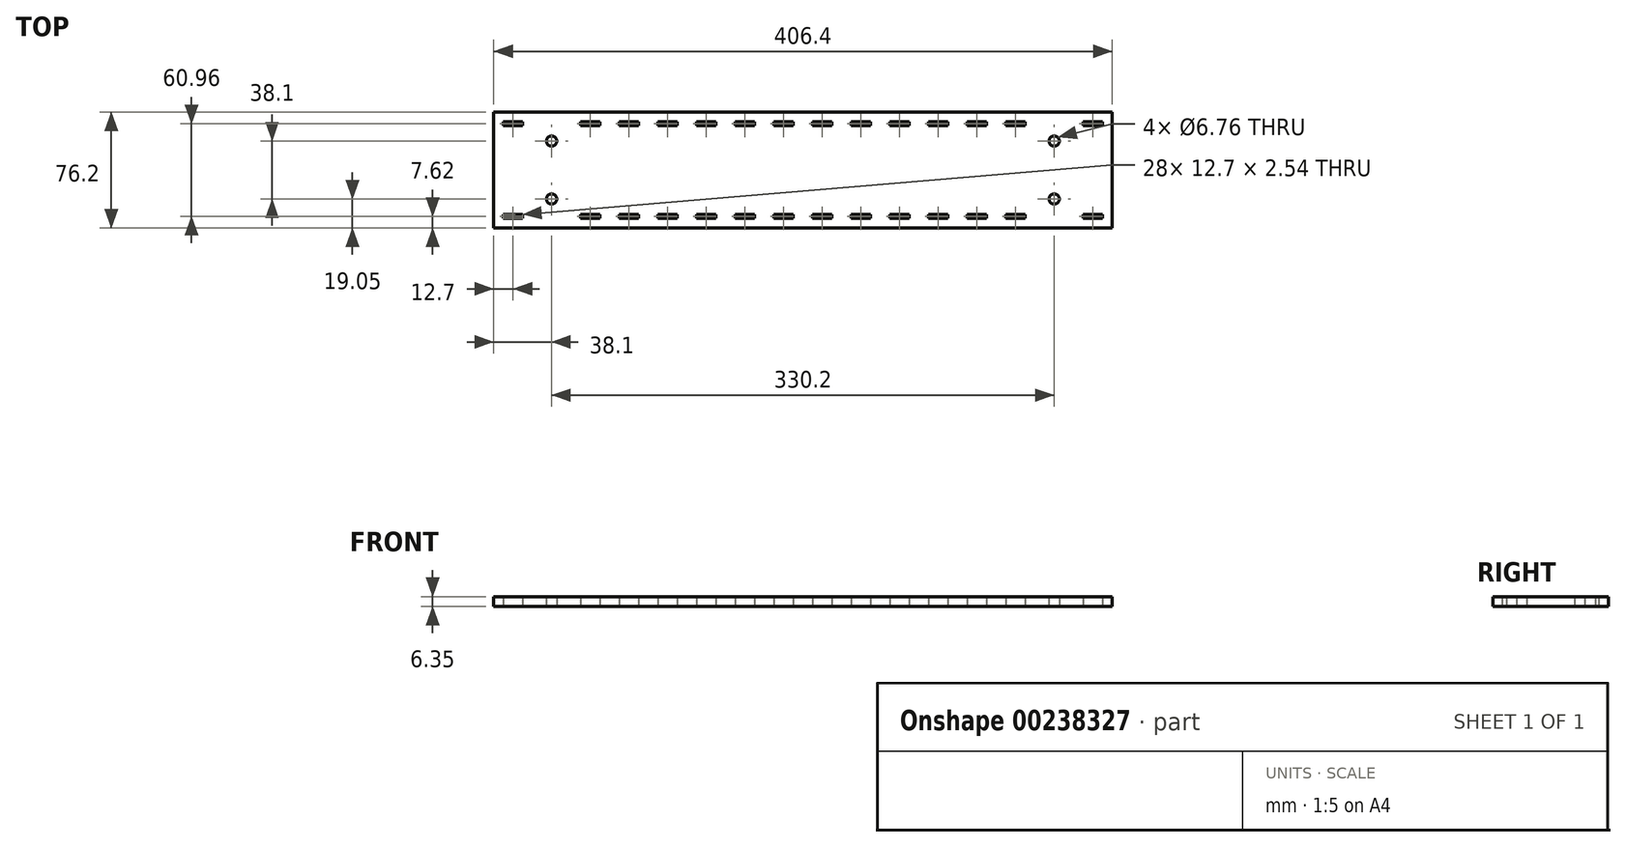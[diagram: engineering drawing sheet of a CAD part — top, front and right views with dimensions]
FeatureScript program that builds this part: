
annotation { "Feature Type Name" : "Feature", "Feature Type Description" : "" }
export const myFeature = defineFeature(function(context is Context, id is Id, definition is map)
    precondition{}
    {
        {
            var Q0;
            Q0=qCreatedBy(makeId("Top.planeOp"),FACE);
            var sketch = newSketch(context, id + "F0", { "sketchPlane" : qUnion([Q0])});
            skLineSegment(sketch, "E0.bottom", {"start": v(0, 0) * mm, "end": v(406.4, 0) * mm});
            skLineSegment(sketch, "E0.top", {"start": v(0, 76.2) * mm, "end": v(406.4, 76.2) * mm});
            skLineSegment(sketch, "E0.left", {"start": v(0, 0) * mm, "end": v(0, 76.2) * mm});
            skLineSegment(sketch, "E0.right", {"start": v(406.4, 0) * mm, "end": v(406.4, 76.2) * mm});
            skCircle(sketch, "E1", {"center": v(38.1, 57.15) * mm, "radius": 3.38 * mm});
            skCircle(sketch, "E2", {"center": v(368.3, 57.15) * mm, "radius": 3.38 * mm});
            skCircle(sketch, "E3.MirrorC", {"center": v(38.1, 19.05) * mm, "radius": 3.38 * mm});
            skCircle(sketch, "E4.MirrorC", {"center": v(368.3, 19.05) * mm, "radius": 3.38 * mm});
            skLineSegment(sketch, "E5", {"start": v(0, 76.2) * mm, "end": v(0, 69.85) * mm});
            skLineSegment(sketch, "E6", {"start": v(6.35, 69.85) * mm, "end": v(6.35, 67.31) * mm});
            skLineSegment(sketch, "E7", {"start": v(6.35, 67.31) * mm, "end": v(19.05, 67.31) * mm});
            skLineSegment(sketch, "E8", {"start": v(19.05, 67.31) * mm, "end": v(19.05, 69.85) * mm});
            skLineSegment(sketch, "E9", {"start": v(19.05, 69.85) * mm, "end": v(6.35, 69.85) * mm});
            skPoint(sketch, "E10.orphan", {"position": v(6.35, 64.77) * mm});
            skLineSegment(sketch, "E11.2.0.0", {"start": v(69.85, 69.85) * mm, "end": v(57.15, 69.85) * mm});
            skLineSegment(sketch, "E11.2.0.1", {"start": v(57.15, 69.85) * mm, "end": v(57.15, 67.31) * mm});
            skLineSegment(sketch, "E11.2.0.2", {"start": v(57.15, 67.31) * mm, "end": v(69.85, 67.31) * mm});
            skLineSegment(sketch, "E11.2.0.3", {"start": v(69.85, 67.31) * mm, "end": v(69.85, 69.85) * mm});
            skLineSegment(sketch, "E11.3.0.0", {"start": v(95.25, 69.85) * mm, "end": v(82.55, 69.85) * mm});
            skLineSegment(sketch, "E11.3.0.1", {"start": v(82.55, 69.85) * mm, "end": v(82.55, 67.31) * mm});
            skLineSegment(sketch, "E11.3.0.2", {"start": v(82.55, 67.31) * mm, "end": v(95.25, 67.31) * mm});
            skLineSegment(sketch, "E11.3.0.3", {"start": v(95.25, 67.31) * mm, "end": v(95.25, 69.85) * mm});
            skLineSegment(sketch, "E11.4.0.0", {"start": v(120.65, 69.85) * mm, "end": v(107.95, 69.85) * mm});
            skLineSegment(sketch, "E11.4.0.1", {"start": v(107.95, 69.85) * mm, "end": v(107.95, 67.31) * mm});
            skLineSegment(sketch, "E11.4.0.2", {"start": v(107.95, 67.31) * mm, "end": v(120.65, 67.31) * mm});
            skLineSegment(sketch, "E11.4.0.3", {"start": v(120.65, 67.31) * mm, "end": v(120.65, 69.85) * mm});
            skLineSegment(sketch, "E11.5.0.0", {"start": v(146.05, 69.85) * mm, "end": v(133.35, 69.85) * mm});
            skLineSegment(sketch, "E11.5.0.1", {"start": v(133.35, 69.85) * mm, "end": v(133.35, 67.31) * mm});
            skLineSegment(sketch, "E11.5.0.2", {"start": v(133.35, 67.31) * mm, "end": v(146.05, 67.31) * mm});
            skLineSegment(sketch, "E11.5.0.3", {"start": v(146.05, 67.31) * mm, "end": v(146.05, 69.85) * mm});
            skLineSegment(sketch, "E11.6.0.0", {"start": v(171.45, 69.85) * mm, "end": v(158.75, 69.85) * mm});
            skLineSegment(sketch, "E11.6.0.1", {"start": v(158.75, 69.85) * mm, "end": v(158.75, 67.31) * mm});
            skLineSegment(sketch, "E11.6.0.2", {"start": v(158.75, 67.31) * mm, "end": v(171.45, 67.31) * mm});
            skLineSegment(sketch, "E11.6.0.3", {"start": v(171.45, 67.31) * mm, "end": v(171.45, 69.85) * mm});
            skLineSegment(sketch, "E11.7.0.0", {"start": v(196.85, 69.85) * mm, "end": v(184.15, 69.85) * mm});
            skLineSegment(sketch, "E11.7.0.1", {"start": v(184.15, 69.85) * mm, "end": v(184.15, 67.31) * mm});
            skLineSegment(sketch, "E11.7.0.2", {"start": v(184.15, 67.31) * mm, "end": v(196.85, 67.31) * mm});
            skLineSegment(sketch, "E11.7.0.3", {"start": v(196.85, 67.31) * mm, "end": v(196.85, 69.85) * mm});
            skLineSegment(sketch, "E11.8.0.0", {"start": v(222.25, 69.85) * mm, "end": v(209.55, 69.85) * mm});
            skLineSegment(sketch, "E11.8.0.1", {"start": v(209.55, 69.85) * mm, "end": v(209.55, 67.31) * mm});
            skLineSegment(sketch, "E11.8.0.2", {"start": v(209.55, 67.31) * mm, "end": v(222.25, 67.31) * mm});
            skLineSegment(sketch, "E11.8.0.3", {"start": v(222.25, 67.31) * mm, "end": v(222.25, 69.85) * mm});
            skLineSegment(sketch, "E11.9.0.0", {"start": v(247.65, 69.85) * mm, "end": v(234.95, 69.85) * mm});
            skLineSegment(sketch, "E11.9.0.1", {"start": v(234.95, 69.85) * mm, "end": v(234.95, 67.31) * mm});
            skLineSegment(sketch, "E11.9.0.2", {"start": v(234.95, 67.31) * mm, "end": v(247.65, 67.31) * mm});
            skLineSegment(sketch, "E11.9.0.3", {"start": v(247.65, 67.31) * mm, "end": v(247.65, 69.85) * mm});
            skLineSegment(sketch, "E11.10.0.0", {"start": v(273.05, 69.85) * mm, "end": v(260.35, 69.85) * mm});
            skLineSegment(sketch, "E11.10.0.1", {"start": v(260.35, 69.85) * mm, "end": v(260.35, 67.31) * mm});
            skLineSegment(sketch, "E11.10.0.2", {"start": v(260.35, 67.31) * mm, "end": v(273.05, 67.31) * mm});
            skLineSegment(sketch, "E11.10.0.3", {"start": v(273.05, 67.31) * mm, "end": v(273.05, 69.85) * mm});
            skLineSegment(sketch, "E11.11.0.0", {"start": v(298.45, 69.85) * mm, "end": v(285.75, 69.85) * mm});
            skLineSegment(sketch, "E11.11.0.1", {"start": v(285.75, 69.85) * mm, "end": v(285.75, 67.31) * mm});
            skLineSegment(sketch, "E11.11.0.2", {"start": v(285.75, 67.31) * mm, "end": v(298.45, 67.31) * mm});
            skLineSegment(sketch, "E11.11.0.3", {"start": v(298.45, 67.31) * mm, "end": v(298.45, 69.85) * mm});
            skLineSegment(sketch, "E11.12.0.0", {"start": v(323.85, 69.85) * mm, "end": v(311.15, 69.85) * mm});
            skLineSegment(sketch, "E11.12.0.1", {"start": v(311.15, 69.85) * mm, "end": v(311.15, 67.31) * mm});
            skLineSegment(sketch, "E11.12.0.2", {"start": v(311.15, 67.31) * mm, "end": v(323.85, 67.31) * mm});
            skLineSegment(sketch, "E11.12.0.3", {"start": v(323.85, 67.31) * mm, "end": v(323.85, 69.85) * mm});
            skLineSegment(sketch, "E11.13.0.0", {"start": v(349.25, 69.85) * mm, "end": v(336.55, 69.85) * mm});
            skLineSegment(sketch, "E11.13.0.1", {"start": v(336.55, 69.85) * mm, "end": v(336.55, 67.31) * mm});
            skLineSegment(sketch, "E11.13.0.2", {"start": v(336.55, 67.31) * mm, "end": v(349.25, 67.31) * mm});
            skLineSegment(sketch, "E11.13.0.3", {"start": v(349.25, 67.31) * mm, "end": v(349.25, 69.85) * mm});
            skLineSegment(sketch, "E12.0.15.0", {"start": v(400.05, 69.85) * mm, "end": v(387.35, 69.85) * mm});
            skLineSegment(sketch, "E12.3.15.0", {"start": v(387.35, 69.85) * mm, "end": v(387.35, 67.31) * mm});
            skLineSegment(sketch, "E12.6.15.0", {"start": v(387.35, 67.31) * mm, "end": v(400.05, 67.31) * mm});
            skLineSegment(sketch, "E12.9.15.0", {"start": v(400.05, 67.31) * mm, "end": v(400.05, 69.85) * mm});
            skLineSegment(sketch, "E13.MirrorCS", {"start": v(285.75, 6.35) * mm, "end": v(285.75, 8.89) * mm});
            skLineSegment(sketch, "E14.MirrorCS", {"start": v(158.75, 6.35) * mm, "end": v(158.75, 8.89) * mm});
            skLineSegment(sketch, "E15.MirrorCS", {"start": v(260.35, 6.35) * mm, "end": v(260.35, 8.89) * mm});
            skLineSegment(sketch, "E16.MirrorCS", {"start": v(107.95, 6.35) * mm, "end": v(107.95, 8.89) * mm});
            skLineSegment(sketch, "E17.MirrorCS", {"start": v(387.35, 6.35) * mm, "end": v(387.35, 8.89) * mm});
            skLineSegment(sketch, "E18.MirrorCS", {"start": v(273.05, 8.89) * mm, "end": v(273.05, 6.35) * mm});
            skLineSegment(sketch, "E19.MirrorCS", {"start": v(171.45, 8.89) * mm, "end": v(171.45, 6.35) * mm});
            skLineSegment(sketch, "E20.MirrorCS", {"start": v(323.85, 8.89) * mm, "end": v(323.85, 6.35) * mm});
            skLineSegment(sketch, "E21.MirrorCS", {"start": v(222.25, 8.89) * mm, "end": v(222.25, 6.35) * mm});
            skLineSegment(sketch, "E22.MirrorCS", {"start": v(120.65, 8.89) * mm, "end": v(120.65, 6.35) * mm});
            skLineSegment(sketch, "E23.MirrorCS", {"start": v(336.55, 6.35) * mm, "end": v(336.55, 8.89) * mm});
            skLineSegment(sketch, "E24.MirrorCS", {"start": v(400.05, 8.89) * mm, "end": v(400.05, 6.35) * mm});
            skLineSegment(sketch, "E25.MirrorCS", {"start": v(234.95, 6.35) * mm, "end": v(234.95, 8.89) * mm});
            skLineSegment(sketch, "E26.MirrorCS", {"start": v(133.35, 6.35) * mm, "end": v(133.35, 8.89) * mm});
            skLineSegment(sketch, "E27.MirrorCS", {"start": v(82.55, 6.35) * mm, "end": v(82.55, 8.89) * mm});
            skLineSegment(sketch, "E28.MirrorCS", {"start": v(184.15, 6.35) * mm, "end": v(184.15, 8.89) * mm});
            skLineSegment(sketch, "E29.MirrorCS", {"start": v(209.55, 6.35) * mm, "end": v(209.55, 8.89) * mm});
            skLineSegment(sketch, "E30.MirrorCS", {"start": v(95.25, 8.89) * mm, "end": v(95.25, 6.35) * mm});
            skLineSegment(sketch, "E31.MirrorCS", {"start": v(247.65, 8.89) * mm, "end": v(247.65, 6.35) * mm});
            skLineSegment(sketch, "E32.MirrorCS", {"start": v(146.05, 8.89) * mm, "end": v(146.05, 6.35) * mm});
            skLineSegment(sketch, "E33.MirrorCS", {"start": v(298.45, 8.89) * mm, "end": v(298.45, 6.35) * mm});
            skLineSegment(sketch, "E34.MirrorCS", {"start": v(196.85, 8.89) * mm, "end": v(196.85, 6.35) * mm});
            skLineSegment(sketch, "E35.MirrorCS", {"start": v(349.25, 8.89) * mm, "end": v(349.25, 6.35) * mm});
            skLineSegment(sketch, "E36.MirrorCS", {"start": v(311.15, 6.35) * mm, "end": v(311.15, 8.89) * mm});
            skLineSegment(sketch, "E37.MirrorCS", {"start": v(400.05, 6.35) * mm, "end": v(387.35, 6.35) * mm});
            skLineSegment(sketch, "E38.MirrorCS", {"start": v(260.35, 8.89) * mm, "end": v(273.05, 8.89) * mm});
            skLineSegment(sketch, "E39.MirrorCS", {"start": v(158.75, 8.89) * mm, "end": v(171.45, 8.89) * mm});
            skLineSegment(sketch, "E40.MirrorCS", {"start": v(311.15, 8.89) * mm, "end": v(323.85, 8.89) * mm});
            skLineSegment(sketch, "E41.MirrorCS", {"start": v(209.55, 8.89) * mm, "end": v(222.25, 8.89) * mm});
            skLineSegment(sketch, "E42.MirrorCS", {"start": v(107.95, 8.89) * mm, "end": v(120.65, 8.89) * mm});
            skLineSegment(sketch, "E43.MirrorCS", {"start": v(387.35, 8.89) * mm, "end": v(400.05, 8.89) * mm});
            skLineSegment(sketch, "E44.MirrorCS", {"start": v(349.25, 6.35) * mm, "end": v(336.55, 6.35) * mm});
            skLineSegment(sketch, "E45.MirrorCS", {"start": v(247.65, 6.35) * mm, "end": v(234.95, 6.35) * mm});
            skLineSegment(sketch, "E46.MirrorCS", {"start": v(146.05, 6.35) * mm, "end": v(133.35, 6.35) * mm});
            skLineSegment(sketch, "E47.MirrorCS", {"start": v(95.25, 6.35) * mm, "end": v(82.55, 6.35) * mm});
            skLineSegment(sketch, "E48.MirrorCS", {"start": v(298.45, 6.35) * mm, "end": v(285.75, 6.35) * mm});
            skLineSegment(sketch, "E49.MirrorCS", {"start": v(196.85, 6.35) * mm, "end": v(184.15, 6.35) * mm});
            skLineSegment(sketch, "E50.MirrorCS", {"start": v(336.55, 8.89) * mm, "end": v(349.25, 8.89) * mm});
            skLineSegment(sketch, "E51.MirrorCS", {"start": v(234.95, 8.89) * mm, "end": v(247.65, 8.89) * mm});
            skLineSegment(sketch, "E52.MirrorCS", {"start": v(133.35, 8.89) * mm, "end": v(146.05, 8.89) * mm});
            skLineSegment(sketch, "E53.MirrorCS", {"start": v(285.75, 8.89) * mm, "end": v(298.45, 8.89) * mm});
            skLineSegment(sketch, "E54.MirrorCS", {"start": v(184.15, 8.89) * mm, "end": v(196.85, 8.89) * mm});
            skLineSegment(sketch, "E55.MirrorCS", {"start": v(82.55, 8.89) * mm, "end": v(95.25, 8.89) * mm});
            skLineSegment(sketch, "E56.MirrorCS", {"start": v(273.05, 6.35) * mm, "end": v(260.35, 6.35) * mm});
            skLineSegment(sketch, "E57.MirrorCS", {"start": v(171.45, 6.35) * mm, "end": v(158.75, 6.35) * mm});
            skLineSegment(sketch, "E58.MirrorCS", {"start": v(120.65, 6.35) * mm, "end": v(107.95, 6.35) * mm});
            skLineSegment(sketch, "E59.MirrorCS", {"start": v(222.25, 6.35) * mm, "end": v(209.55, 6.35) * mm});
            skLineSegment(sketch, "E60.MirrorCS", {"start": v(323.85, 6.35) * mm, "end": v(311.15, 6.35) * mm});
            skLineSegment(sketch, "E61.MirrorCS", {"start": v(19.05, 6.35) * mm, "end": v(6.35, 6.35) * mm});
            skLineSegment(sketch, "E62.MirrorCS", {"start": v(19.05, 8.89) * mm, "end": v(19.05, 6.35) * mm});
            skLineSegment(sketch, "E63.MirrorCS", {"start": v(57.15, 6.35) * mm, "end": v(57.15, 8.89) * mm});
            skLineSegment(sketch, "E64.MirrorCS", {"start": v(69.85, 6.35) * mm, "end": v(57.15, 6.35) * mm});
            skLineSegment(sketch, "E65.MirrorCS", {"start": v(6.35, 8.89) * mm, "end": v(19.05, 8.89) * mm});
            skLineSegment(sketch, "E66.MirrorCS", {"start": v(69.85, 8.89) * mm, "end": v(69.85, 6.35) * mm});
            skLineSegment(sketch, "E67.MirrorCS", {"start": v(57.15, 8.89) * mm, "end": v(69.85, 8.89) * mm});
            skLineSegment(sketch, "E68.MirrorCS", {"start": v(6.35, 6.35) * mm, "end": v(6.35, 8.89) * mm});
            skPoint(sketch, "E69.MirrorP", {"position": v(6.35, 11.43) * mm});
            skSolve(sketch);
        }
        {
            var Q0;
            Q0 = qSketchRegion(id + "F0", true);
            extrude(context, id + "F1", {"entities" : qUnion([Q0]), "depth" : 6.35 * mm});
        }
    });
